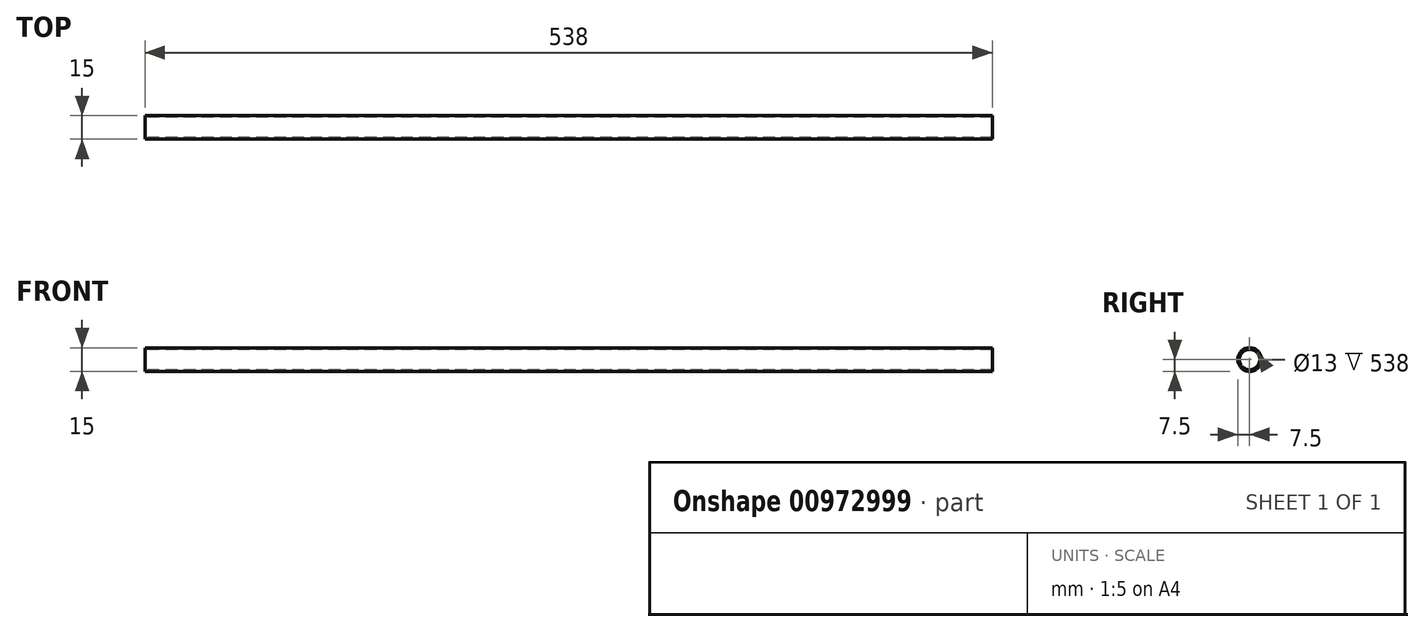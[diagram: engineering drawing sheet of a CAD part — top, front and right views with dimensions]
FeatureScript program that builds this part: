
annotation { "Feature Type Name" : "Feature", "Feature Type Description" : "" }
export const myFeature = defineFeature(function(context is Context, id is Id, definition is map)
    precondition{}
    {
        {
            var Q0;
            Q0=qCreatedBy(makeId("Right.planeOp"),FACE);
            var sketch = newSketch(context, id + "F0", { "sketchPlane" : qUnion([Q0])});
            skCircle(sketch, "E0", {"center": v(0, 0) * mm, "radius": 7.5 * mm});
            skCircle(sketch, "E1", {"center": v(0, 0) * mm, "radius": 6.5 * mm});
            skSolve(sketch);
        }
        {
            var Q0;
            Q0 = qSketchRegion(id + "F0", true);
            extrude(context, id + "F1", {"entities" : qUnion([Q0]), "depth" : 269 * mm, "offsetDistance" : 25 * mm, "hasSecondDirection" : true, "secondDirectionOppositeDirection" : true, "secondDirectionDepth" : 269 * mm});
        }
    });
